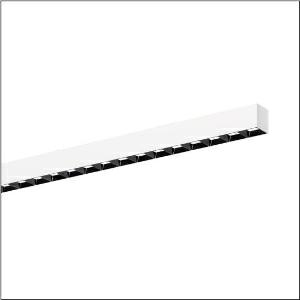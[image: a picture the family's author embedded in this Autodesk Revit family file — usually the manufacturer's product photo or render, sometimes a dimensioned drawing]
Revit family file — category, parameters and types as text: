
# Revit family: silica_r__21_51mx24tat4w_113b
name_source: partatom
category: Lighting Fixtures
units: mm (PartAtom-declared; Revit-internal decimal feet)

## family parameters
Cut with Voids When Loaded = No
Host = Face
Light Source = No
Part Type = Normal
Room Calculation Point = No
Round Connector Dimension = Use Diameter
Shared = No

## types (1)
- --- (1 x LED, 3280 lm, 32.4 W, 6500K)
    Apparent Load = 32 VA
    CIE Flux Codes = 74 94 99 100 100
    Color Rendering = 80
    Color Temperature = 6500K
    Default Elevation = 1800 mm
    Description = Silica® 21, office luminaire, primary light control with darklight reflector, of PMMA, black, light emission: direct distribution, primary light characteristic: asymmetric, installation type: surface-mounted, LED, rated luminous flux: 3.280lm, luminous efficacy: 96lm/W, light colour: 8tw, colour temperature: 2700..6500K, control gear: ECG DALI, with terminal, 3+2-pole, max. 2.5mm², mains connection: 220..240V, AC, 50/60Hz, rated input power: 34.1W, luminaire housing, of aluminium, traffic white (RAL 9016), length: 1.204mm, width: 53mm, height: 53mm, protection rating (complete): IP20, insulation class (complete): insulation class I (protective earthing), certification: CE, permissible operating ambient temperature: 0..+35°C, standard: EN 50419, packaging unit: 1 piece
    Height = 0 mm  [stored 0 ft]
    Lamp = 1 x LED
    Lamp Light Flux = 3280 lm
    Lamp Power = 32.4 W
    Lamp count = 1
    Length = 1204 mm
    Luminous efficacy = 101 lm/W
    Manufacturer = Siteco
    ModVariant = No
    Model = 51MX24TAT4W
    Mounting Place = Ceiling
    Mounting Type = Recessed
    Number of Poles = 1
    OnlyDefault = Yes
    Power Factor = 1
    Product Name = Silica® 21
    Product group = office luminaire | ceiling recessed
    ProductGroupID = 401
    Protection Class = Protection class I
    Protection Degree = IP 20
    RLX_Detail_Level = 1
    RLX_Emergency_Light_Flux = 0 lm
    RLX_Emergency_Type = 0
    RLX_Emergency_Type_DB = No
    RlxData = <blob elided: 38417 chars, md5=9bd05ee7>
    Socket = socket
    Standby Power = 0 W
    System Light Flux = 3280 lm
    System Power = 32 W
    Type Comments = individual setting
    Type Image = l_1297779.jpg
    URL = http://relux.com
    VarID = @adj_071341
    Voltage = 0 V
    Weight = 0.00 kg
    Width = 53 mm

note: [stored X ft] marks values corroborated as IEEE doubles in the binary element streams (Revit-internal decimal feet)

## geometry (parser evidence)
native form markers: Blend x4, Sweep x10
no freeform markers — native parametric forms only
